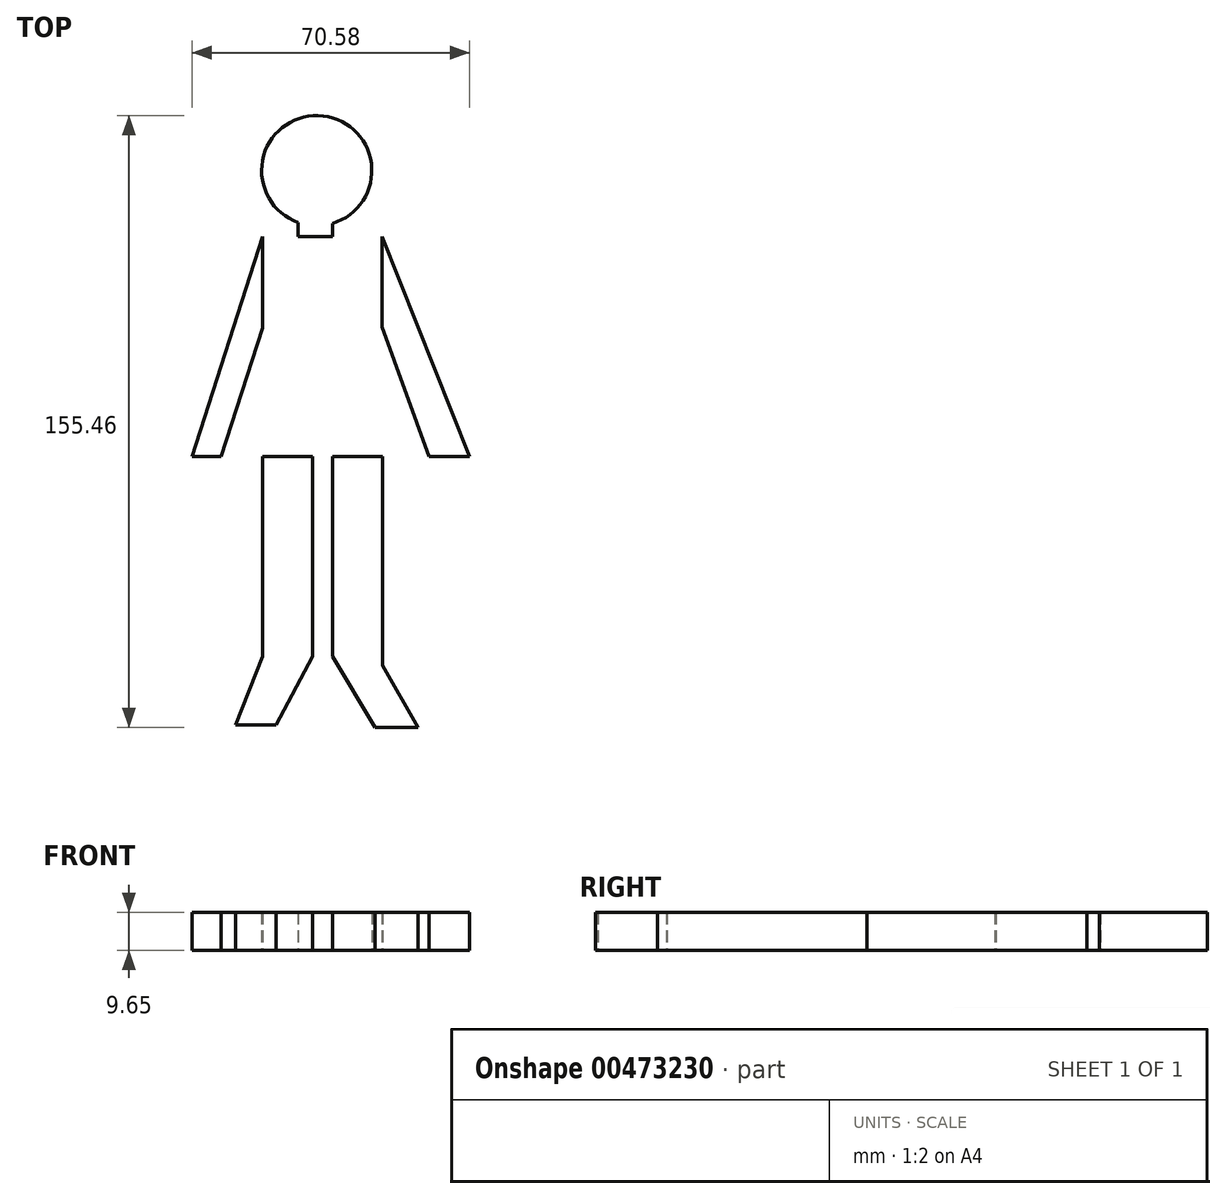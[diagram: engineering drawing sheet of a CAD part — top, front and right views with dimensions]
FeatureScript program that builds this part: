
annotation { "Feature Type Name" : "Feature", "Feature Type Description" : "" }
export const myFeature = defineFeature(function(context is Context, id is Id, definition is map)
    precondition{}
    {
        {
            var Q0;
            Q0=qCreatedBy(makeId("Top.planeOp"),FACE);
            var sketch = newSketch(context, id + "F0", { "sketchPlane" : qUnion([Q0])});
            skLineSegment(sketch, "E0.bottom", {"start": v(0, 0) * mm, "end": v(12.7, 0) * mm});
            skLineSegment(sketch, "E0.top", {"start": v(0, -50.8) * mm, "end": v(12.7, -50.8) * mm});
            skLineSegment(sketch, "E0.left", {"start": v(0, 0) * mm, "end": v(0, -50.8) * mm});
            skLineSegment(sketch, "E0.right", {"start": v(12.7, 0) * mm, "end": v(12.7, -50.8) * mm});
            skLineSegment(sketch, "E1", {"start": v(0, -50.8) * mm, "end": v(10.86, -68.87) * mm});
            skLineSegment(sketch, "E2", {"start": v(10.86, -68.87) * mm, "end": v(21.72, -68.87) * mm});
            skLineSegment(sketch, "E3", {"start": v(12.7, -53.15) * mm, "end": v(21.72, -68.87) * mm});
            skLineSegment(sketch, "E4.right", {"start": v(-5.08, 0) * mm, "end": v(-5.08, -50.8) * mm});
            skLineSegment(sketch, "E5.bottom", {"start": v(-5.08, 0) * mm, "end": v(-17.78, 0) * mm});
            skLineSegment(sketch, "E5.top", {"start": v(-5.08, -50.86) * mm, "end": v(-17.78, -50.86) * mm});
            skLineSegment(sketch, "E5.left", {"start": v(-5.08, 0) * mm, "end": v(-5.08, -50.86) * mm});
            skLineSegment(sketch, "E5.right", {"start": v(-17.78, 0) * mm, "end": v(-17.78, -50.86) * mm});
            skLineSegment(sketch, "E6.bottom", {"start": v(-17.78, 0) * mm, "end": v(12.57, 0) * mm});
            skLineSegment(sketch, "E6.top", {"start": v(-17.78, 55.88) * mm, "end": v(12.57, 55.88) * mm});
            skLineSegment(sketch, "E6.left", {"start": v(-17.78, 0) * mm, "end": v(-17.78, 55.88) * mm});
            skLineSegment(sketch, "E6.right", {"start": v(12.57, 0) * mm, "end": v(12.57, 55.88) * mm});
            skLineSegment(sketch, "E7", {"start": v(-17.78, 55.88) * mm, "end": v(-35.72, 0) * mm});
            skLineSegment(sketch, "E8", {"start": v(-17.78, 32.58) * mm, "end": v(-28.24, 0) * mm});
            skLineSegment(sketch, "E9", {"start": v(-28.24, 0) * mm, "end": v(-35.72, 0) * mm});
            skLineSegment(sketch, "E10", {"start": v(12.57, 32.86) * mm, "end": v(24.57, 0) * mm});
            skPoint(sketch, "E10.endSnap0", {"position": v(-31.98, 0) * mm});
            skCircle(sketch, "E11", {"center": v(-4, 72.58) * mm, "radius": 14 * mm});
            skLineSegment(sketch, "E12", {"start": v(-8.75, 59.4) * mm, "end": v(-8.75, 55.88) * mm});
            skLineSegment(sketch, "E13", {"start": v(-8.75, 55.88) * mm, "end": v(0, 55.88) * mm});
            skLineSegment(sketch, "E14", {"start": v(0, 55.88) * mm, "end": v(0, 59.16) * mm});
            skPoint(sketch, "E15.end.orphan", {"position": v(30.29, 0) * mm});
            skLineSegment(sketch, "E16", {"start": v(12.57, 55.88) * mm, "end": v(34.86, 0) * mm});
            skLineSegment(sketch, "E17", {"start": v(34.86, 0) * mm, "end": v(24.57, 0) * mm});
            skLineSegment(sketch, "E18", {"start": v(-17.78, -50.86) * mm, "end": v(-24.57, -68.3) * mm});
            skLineSegment(sketch, "E19", {"start": v(-24.57, -68.3) * mm, "end": v(-14.29, -68.3) * mm});
            skLineSegment(sketch, "E20", {"start": v(-14.29, -68.3) * mm, "end": v(-5.08, -50.86) * mm});
            skLineSegment(sketch, "E21", {"start": v(12.7, -53.15) * mm, "end": v(14.34, -56.02) * mm});
            skLineSegment(sketch, "E22", {"start": v(12.7, -53.15) * mm, "end": v(12.7, -50.8) * mm});
            skSolve(sketch);
        }
        {
            var Q0;
            Q0=makeQuery(id+"F0.imprint","IMPRINT",FACE,{"disambiguationData":[TD([[makeQuery(id+"F0.imprint","IMPRINT",EDGE,{"derivedFrom":sQuery(id+"F0.wireOp",EDGE,"E0.top")}),-1.0]])]});
            var Q1;
            Q1=makeQuery(id+"F0.imprint","IMPRINT",FACE,{"disambiguationData":[TD([[makeQuery(id+"F0.imprint","IMPRINT",EDGE,{"derivedFrom":sQuery(id+"F0.wireOp",EDGE,"E5.top")}),1.0]])]});
            var Q2;
            {var subQ0=sQuery(id+"F0.wireOp",EDGE,"E7");Q2=makeQuery(id+"F0.imprint","IMPRINT",FACE,{"disambiguationData":[TD([[makeQuery(id+"F0.imprint","IMPRINT",EDGE,{"derivedFrom":subQ0}),1.0]])]});}
            var Q3;
            {var subQ2=sQuery(id+"F0.wireOp",EDGE,"E10");Q3=makeQuery(id+"F0.imprint","IMPRINT",FACE,{"disambiguationData":[TD([[makeQuery(id+"F0.imprint","IMPRINT",EDGE,{"derivedFrom":subQ2}),1.0]])]});}
            var Q4;
            {var subQ0=sQuery(id+"F0.wireOp",EDGE,"E11");var subQ1=makeQuery(id+"F0.imprint","INTERSECT",VERTEX,{"derivedFrom":[subQ0,sQuery(id+"F0.wireOp",EDGE,"E12")]});Q4=makeQuery(id+"F0.imprint","IMPRINT",FACE,{"disambiguationData":[TD([[makeQuery(id+"F0.imprint","IMPRINT",EDGE,{"disambiguationData":[TD([[subQ1,-1.0]])],"derivedFrom":subQ0}),1.0]])]});}
            var Q5;
            {var subQ2=sQuery(id+"F0.wireOp",EDGE,"E0.bottom");Q5=makeQuery(id+"F0.imprint","IMPRINT",FACE,{"disambiguationData":[TD([[makeQuery(id+"F0.imprint","IMPRINT",EDGE,{"derivedFrom":subQ2}),-1.0]])]});}
            var Q6;
            {var subQ0=sQuery(id+"F0.wireOp",EDGE,"E5.top");Q6=makeQuery(id+"F0.imprint","IMPRINT",FACE,{"disambiguationData":[TD([[makeQuery(id+"F0.imprint","IMPRINT",EDGE,{"derivedFrom":subQ0}),-1.0]])]});}
            var Q7;
            {var subQ0=sQuery(id+"F0.wireOp",EDGE,"E12");Q7=makeQuery(id+"F0.imprint","IMPRINT",FACE,{"disambiguationData":[TD([[makeQuery(id+"F0.imprint","IMPRINT",EDGE,{"derivedFrom":subQ0}),1.0]])]});}
            extrude(context, id + "F1", {"entities" : qUnion([Q0, Q1, Q2, Q3, Q4, Q5, Q6, Q7]), "depth" : 9.65 * mm});
        }
    });
